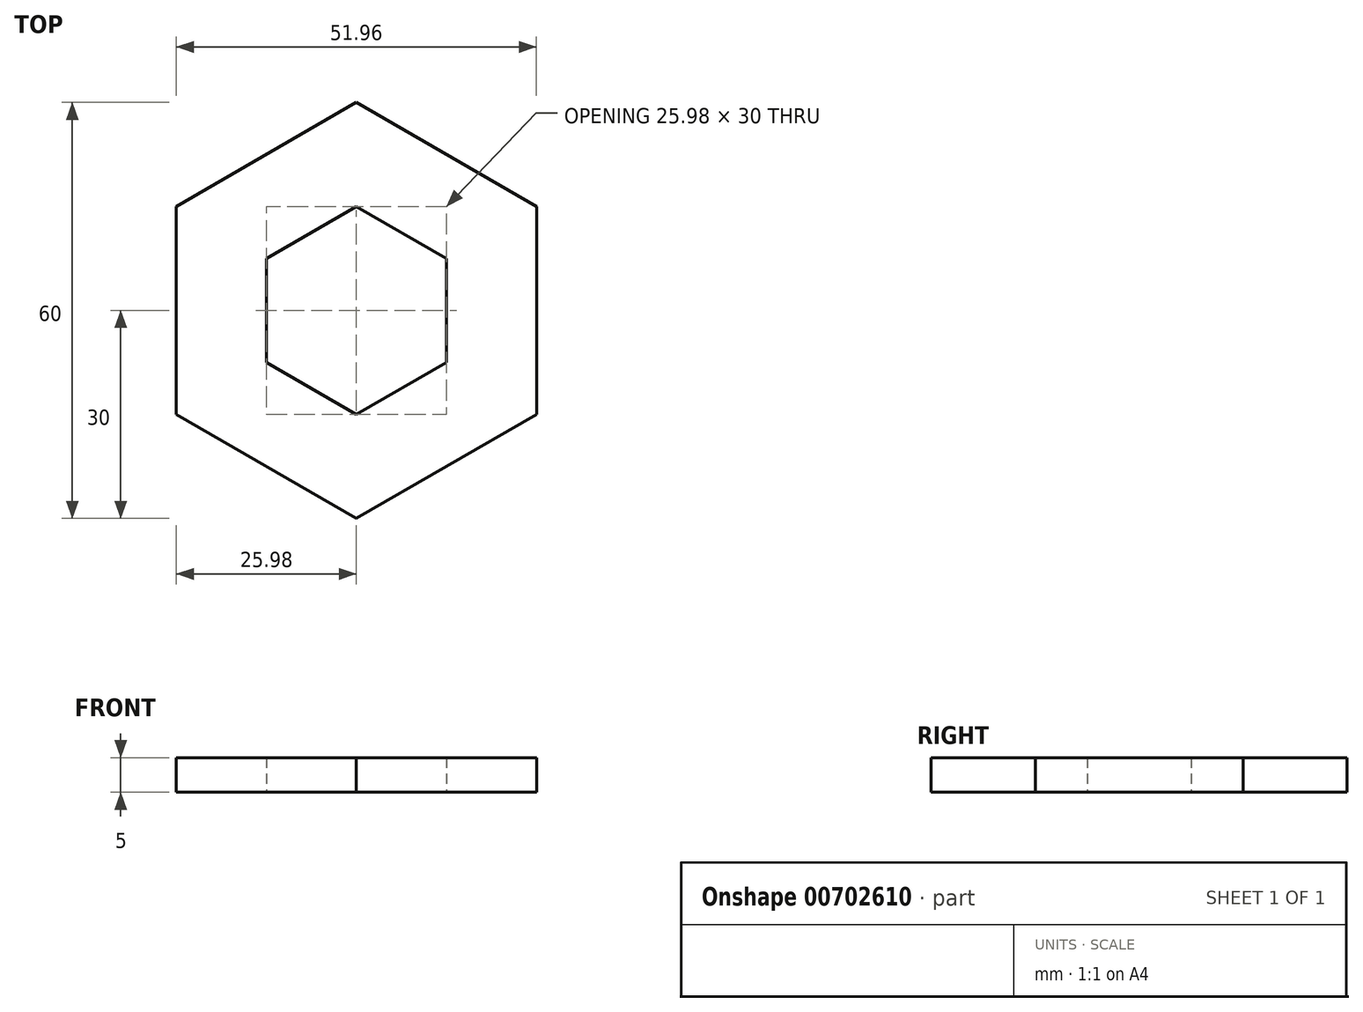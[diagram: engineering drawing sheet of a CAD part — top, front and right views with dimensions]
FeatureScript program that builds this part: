
annotation { "Feature Type Name" : "Feature", "Feature Type Description" : "" }
export const myFeature = defineFeature(function(context is Context, id is Id, definition is map)
    precondition{}
    {
        {
            var Q0;
            Q0=qCreatedBy(makeId("Top.planeOp"),FACE);
            var sketch = newSketch(context, id + "F0", { "sketchPlane" : qUnion([Q0])});
            skCircle(sketch, "E0.cCircle", {"center": v(0, 0) * mm, "radius": 30 * mm, "construction": true});
            skLineSegment(sketch, "E0.0", {"start": v(-25.98, 15) * mm, "end": v(0, 30) * mm});
            skLineSegment(sketch, "E0.1", {"start": v(0, 30) * mm, "end": v(25.98, 15) * mm});
            skLineSegment(sketch, "E0.2", {"start": v(25.98, 15) * mm, "end": v(25.98, -15) * mm});
            skLineSegment(sketch, "E0.3", {"start": v(25.98, -15) * mm, "end": v(0, -30) * mm});
            skLineSegment(sketch, "E0.4", {"start": v(0, -30) * mm, "end": v(-25.98, -15) * mm});
            skLineSegment(sketch, "E0.5", {"start": v(-25.98, -15) * mm, "end": v(-25.98, 15) * mm});
            skCircle(sketch, "E1.cCircle", {"center": v(0, 0) * mm, "radius": 15 * mm, "construction": true});
            skPoint(sketch, "E1.cCircle.perimeterSnap0", {"position": v(-13, 22.5) * mm});
            skLineSegment(sketch, "E1.0", {"start": v(-13, 7.5) * mm, "end": v(0, 15) * mm});
            skPoint(sketch, "E1.0.startSnap0", {"position": v(-13, 22.5) * mm});
            skLineSegment(sketch, "E1.1", {"start": v(0, 15) * mm, "end": v(13, 7.5) * mm});
            skLineSegment(sketch, "E1.2", {"start": v(13, 7.5) * mm, "end": v(13, -7.5) * mm});
            skLineSegment(sketch, "E1.3", {"start": v(13, -7.5) * mm, "end": v(0, -15) * mm});
            skLineSegment(sketch, "E1.4", {"start": v(0, -15) * mm, "end": v(-13, -7.5) * mm});
            skLineSegment(sketch, "E1.5", {"start": v(-13, -7.5) * mm, "end": v(-13, 7.5) * mm});
            skSolve(sketch);
        }
        {
            var Q0;
            Q0=makeQuery(id+"F0.imprint","IMPRINT",FACE,{"disambiguationData":[TD([[makeQuery(id+"F0.imprint","IMPRINT",EDGE,{"derivedFrom":sQuery(id+"F0.wireOp",EDGE,"E0.0")}),-1.0]])]});
            extrude(context, id + "F1", {"entities" : qUnion([Q0]), "endBound" : BoundingType.SYMMETRIC, "depth" : 5 * mm, "offsetDistance" : 25 * mm});
        }
    });
